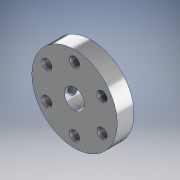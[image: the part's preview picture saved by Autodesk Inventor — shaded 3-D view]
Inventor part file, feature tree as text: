
AUTODESK INVENTOR PART (.ipt)
format: ipt  version: 2016 (Build 200138000, 138)  size: 175,616 bytes
history: native  units: mm
features: extrude x5, sketch x5
ambient origin geometry x8: Origin, YZ Plane, XZ Plane, XY Plane, X Axis, Y Axis, Z Axis, Center Point
bodies: Solid1 (feature_tree)
feature tree (10):
  extrude  "Extrusion1"  Depth=3.0mm
  extrude  "Extrusion2"  Depth=60.0mm TaperAngle=360.0deg
  extrude  "Extrusion3"  Depth=6.0mm
  extrude  "Extrusion4"  Depth=5.0mm
  extrude  "Extrusion5"  TaperAngle=0.0deg  [1 undecoded]
  sketch  "Sketch1"  dims[d0=25.4mm d1=3.0mm]
  sketch  "Sketch2"  dims[d3=9.5mm d4=60.0mm d6=360.0deg]
  sketch  "Sketch3"  dims[d8=5.0mm d9=0.0mm d10=6.0mm]
  sketch  "Sketch5"  dims[d11=5.0mm d12=0.0mm d13=12.0mm]
  sketch  "Sketch6"  dims[d14=4.2mm d15=0.0mm d20=0.0mm d21=3.0mm d22=2.5mm d23=0.0mm d24=4.2mm d25=0.0mm d26=3.0mm d27=7.1mm d28=0.0mm d29=4.2mm d30=0.0mm]
note: 1 required parameter value undecoded (feature->parameter linkage not recoverable at this tier; creation-order binding heuristic only, values carry confidence <= 0.55)
